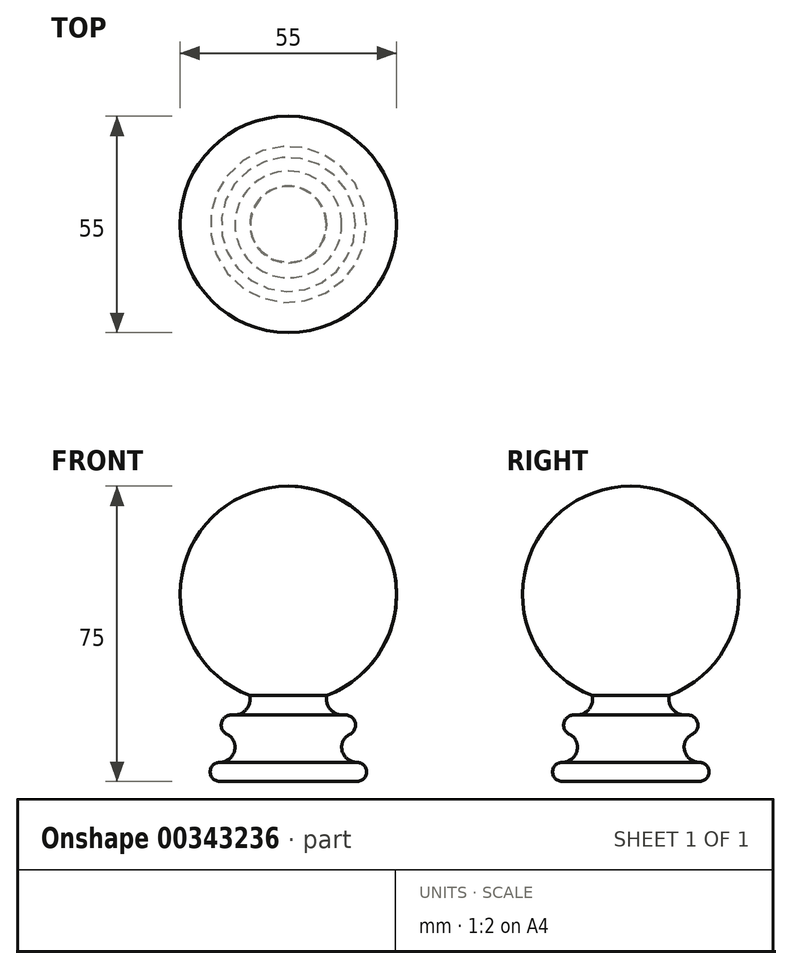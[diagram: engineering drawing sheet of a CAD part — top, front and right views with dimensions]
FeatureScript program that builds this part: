
annotation { "Feature Type Name" : "Feature", "Feature Type Description" : "" }
export const myFeature = defineFeature(function(context is Context, id is Id, definition is map)
    precondition{}
    {
        {
            var Q0;
            Q0=qCreatedBy(makeId("Front.planeOp"),FACE);
            var sketch = newSketch(context, id + "F0", { "sketchPlane" : qUnion([Q0])});
            skArc(sketch, "E0", {"start": v(0, -27.5) * mm, "mid": v(27.5, 0) * mm, "end": v(0, 27.5) * mm});
            skLineSegment(sketch, "E1", {"start": v(0, 27.5) * mm, "end": v(0, -27.5) * mm});
            skLineSegment(sketch, "E2", {"start": v(0, 27.5) * mm, "end": v(0, -47.5) * mm});
            skLineSegment(sketch, "E3", {"start": v(0, -47.5) * mm, "end": v(17.44, -47.5) * mm});
            skArc(sketch, "E4", {"start": v(17.44, -47.5) * mm, "mid": v(19.85, -45.09) * mm, "end": v(17.44, -42.68) * mm});
            skArc(sketch, "E5", {"start": v(17.44, -42.68) * mm, "mid": v(14.69, -41.54) * mm, "end": v(13.55, -38.78) * mm});
            skArc(sketch, "E6", {"start": v(13.55, -38.78) * mm, "mid": v(14.1, -36.88) * mm, "end": v(15.58, -35.56) * mm});
            skArc(sketch, "E7", {"start": v(15.58, -35.56) * mm, "mid": v(16.96, -32.54) * mm, "end": v(14.23, -30.65) * mm});
            skArc(sketch, "E8", {"start": v(14.23, -30.65) * mm, "mid": v(10.75, -29.3) * mm, "end": v(9.77, -25.7) * mm});
            skSolve(sketch);
        }
        {
            var Q0;
            Q0=makeQuery(id+"F0.imprint","IMPRINT",FACE,{"disambiguationData":[TD([[makeQuery(id+"F0.imprint","IMPRINT",EDGE,{"derivedFrom":sQuery(id+"F0.wireOp",EDGE,"E0")}),1.0]])]});
            var Q1;
            {var subQ0=sQuery(id+"F0.wireOp",EDGE,"E3");Q1=makeQuery(id+"F0.imprint","IMPRINT",FACE,{"disambiguationData":[TD([[makeQuery(id+"F0.imprint","IMPRINT",EDGE,{"derivedFrom":subQ0}),1.0]])]});}
            var Q2;
            Q2=sQuery(id+"F0.wireOp",EDGE,"E1");
            revolve(context, id + "F1", {"entities" : qUnion([Q0, Q1]), "axis" : qUnion([Q2]), "revolveType" : RevolveType.FULL});
        }
    });
